# Revit family: Hinge_TCHDRND1S3_TruClose_DD-Technologies-Pair
name_source: partatom
category: Specialty Equipment
units: mm (PartAtom-declared; Revit-internal decimal feet)

## family parameters
Always vertical = Yes
Cut with Voids When Loaded = No
Enable Cutting in Views = No
Maintain Annotation Orientation = No
Part Type = Normal
Room Calculation Point = No
Round Connector Dimension = Use Diameter
Shared = No
Work Plane-Based = Yes

## types (6) — shared parameters
Assembly Code = G2060.20 Fences and Gates
Catalog Page = https://us.ddtech.com
Colors = Black
Default Elevation = 4' - 0"
Fixed Gate Gap = 1" (25mm)
Gate Material = Chainlink
Hinge Material = Reinforced Polymer
Keynote = 32 31 00 Fence & Gates
Manufacturer = D&D Technologies
Maximal Self-Closing Gate Weight*  (per pair of hinge) = 154 lb (70kg)
Model = TCHDRND1S3
Product Webpage with product image = https://us.ddtech.com
Side Legs = Round post adaptors provided
Specification = https://us.ddtech.com
Type = Adjustable self-closing heavy-duty hinge
URL = https://ddtech.com

## per-type parameters (varying)
| type | Adaptor Type | Description | Gate Dia | Gate Hinge Length | Post Dia | Post Hinge Length | Product Name |
| TCHDRND1S3 - Adjustable self-closing heavy-duty hinge - Gate-Diameter-1-3/8"(35mm) Post-Diameter-2"(48-51mm) | Hinge_TCHDRND1S3_TruClose_DD-Technologies : TCHDRND1S3 - Adjustable self-closing heavy-duty hinge - Gate-Diameter-1-3/8"(35mm) Post-Diameter-2"(48-51mm) | Adjustable, self-closing heavy duty hinge, black, with adaptors for 1-3/8” (35mm) gate diameter & 2” (48–51mm) post diameter | 0' - 1 3/8" | 0' - 1 3/8" | 0' - 2" | 0' - 1 1/2" | Truclose® Round Heavy Duty |
| TCHDRND1S3 - Adjustable self-closing heavy-duty hinge - Gate-Diameter-1-3/8"(35mm) Post-Diameter-2-3/8”(60mm) | Hinge_TCHDRND1S3_TruClose_DD-Technologies : TCHDRND1S3 - Adjustable self-closing heavy-duty hinge - Gate-Diameter-1-3/8"(35mm) Post-Diameter-2-3/8”(60mm) | Adjustable, self-closing heavy duty hinge, black, with adaptors for 1-3/8” (35mm) gate diameter & 2-3/8” (60mm) post diameter | 0' - 1 3/8" | 0' - 1 3/8" | 0' - 2 3/8" | 0' - 1 3/4" | Truclose® Round Heavy Duty |
| TCHDRND1S3 - Adjustable self-closing heavy-duty hinge - Gate-Diameter-1-3/8" (35mm) Post-Diameter-2-7/8"(73mm) | Hinge_TCHDRND1S3_TruClose_DD-Technologies : TCHDRND1S3 - Adjustable self-closing heavy-duty hinge - Gate-Diameter-1-3/8" (35mm) Post-Diameter-2-7/8"(73mm) | Adjustable, self-closing heavy duty hinge, black, with adaptors for 1-3/8” (35mm) gate diameter & 2-7/8” (73mm) post diameter | 0' - 1 3/8" | 0' - 1 3/8" | 0' - 2 7/8" | 0' - 2" | TruClose® Round Heavy Duty |
| TCHDRND1S3 - Adjustable self-closing heavy-duty hinge - Gate-Diameter-1-5/8"(41mm) Post-Diameter-2"(48-51mm) | Hinge_TCHDRND1S3_TruClose_DD-Technologies : TCHDRND1S3 - Adjustable self-closing heavy-duty hinge - Gate-Diameter-1-5/8"(41mm) Post-Diameter-2"(48-51mm) | Adjustable, self-closing heavy duty hinge, black, with adaptors for 1-5/8” (41mm) gate diameter & 2” (48–51mm) post diameter | 0' - 1 5/8" | 0' - 1 1/2" | 0' - 2" | 0' - 1 1/2" | Truclose® Round Heavy Duty |
| TCHDRND1S3 - Adjustable self-closing heavy-duty hinge - Gate-Diameter-1-5/8"(41mm) Post-Diameter-2-3/8”(60mm) | Hinge_TCHDRND1S3_TruClose_DD-Technologies : TCHDRND1S3 - Adjustable self-closing heavy-duty hinge - Gate-Diameter-1-5/8"(41mm) Post-Diameter-2-3/8”(60mm) | Adjustable, self-closing heavy duty hinge, black, with adaptors for 1-5/8” (41mm) gate diameter & 2-3/8” (60mm) post diameter | 0' - 1 5/8" | 0' - 1 1/2" | 0' - 2 3/8" | 0' - 1 3/4" | Truclose® Round Heavy Duty |
| TCHDRND1S3 - Adjustable self-closing heavy-duty hinge - Gate-Diameter-1-5/8" (41mm) Post-Diameter-2-7/8"(73mm) | Hinge_TCHDRND1S3_TruClose_DD-Technologies : TCHDRND1S3 - Adjustable self-closing heavy-duty hinge - Gate-Diameter-1-5/8" (41mm) Post-Diameter-2-7/8"(73mm) | Adjustable, self-closing heavy duty hinge, black, with adaptors for 1-5/8” (41mm) gate diameter & 2-7/8” (73mm) post diameter | 0' - 1 5/8" | 0' - 1 1/2" | 0' - 2 7/8" | 0' - 2" | Truclose® Round Heavy Duty |

## geometry (parser evidence)
native form markers: Sweep x9
no freeform markers — native parametric forms only
